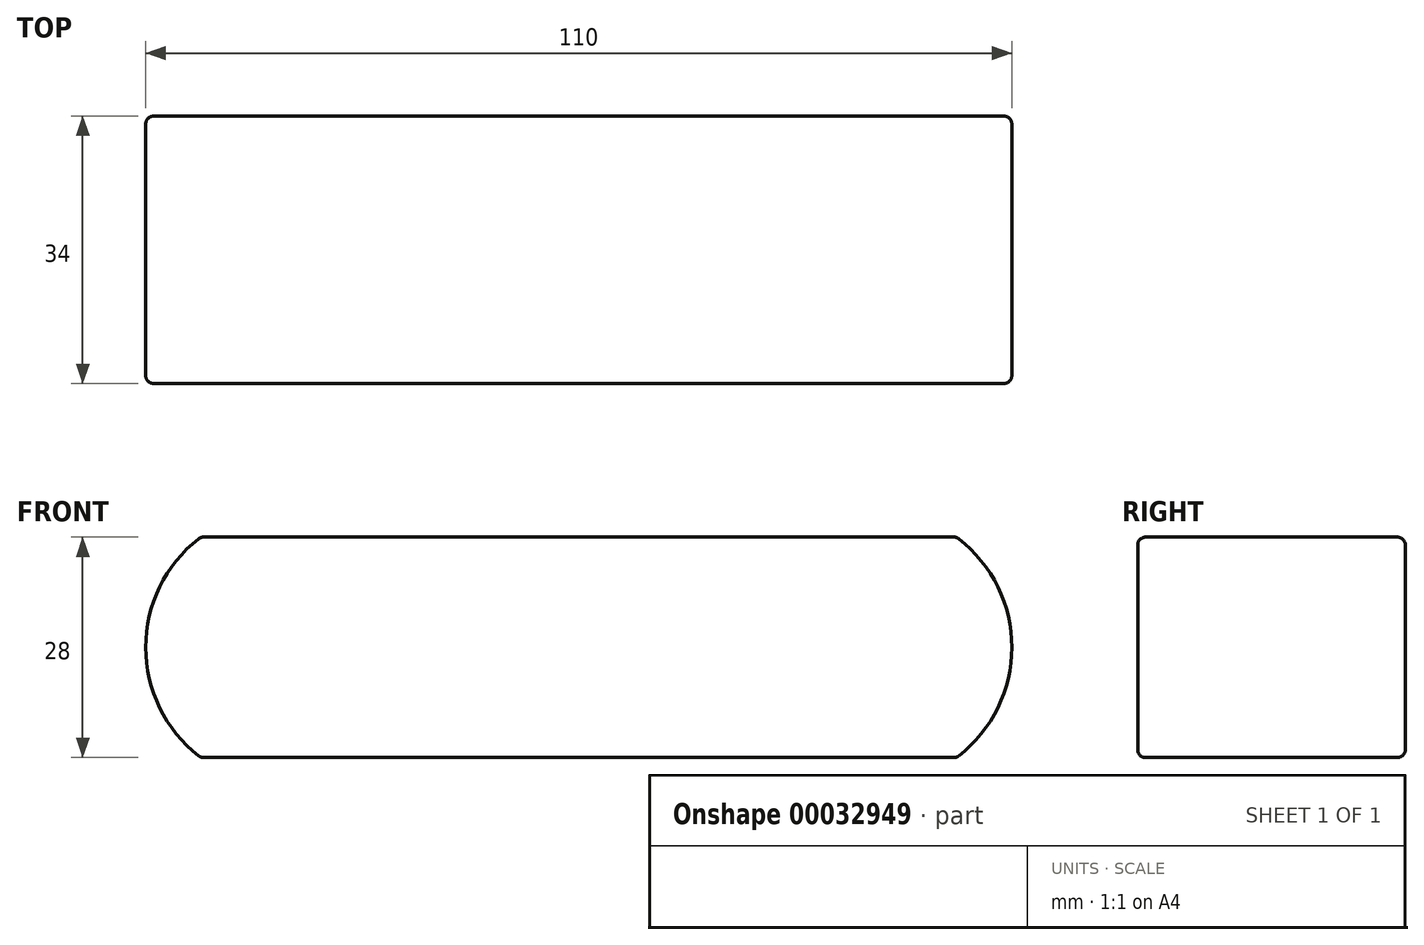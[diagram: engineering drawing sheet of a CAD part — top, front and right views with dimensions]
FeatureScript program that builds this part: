
annotation { "Feature Type Name" : "Feature", "Feature Type Description" : "" }
export const myFeature = defineFeature(function(context is Context, id is Id, definition is map)
    precondition{}
    {
        {
            var Q0;
            Q0=qCreatedBy(makeId("Front.planeOp"),FACE);
            var sketch = newSketch(context, id + "F0", { "sketchPlane" : qUnion([Q0])});
            skLineSegment(sketch, "E0.rect.bottom", {"start": v(48, -14) * mm, "end": v(-48, -14) * mm});
            skLineSegment(sketch, "E0.rect.top", {"start": v(48, 14) * mm, "end": v(-48, 14) * mm});
            skPoint(sketch, "E0.rect.middle", {"position": v(0, 0) * mm});
            skLineSegment(sketch, "E1.rect.bottom", {"start": v(55, -14) * mm, "end": v(-55, -14) * mm, "construction": true});
            skLineSegment(sketch, "E1.rect.top", {"start": v(55, 14) * mm, "end": v(-55, 14) * mm, "construction": true});
            skLineSegment(sketch, "E1.rect.left", {"start": v(55, -14) * mm, "end": v(55, 14) * mm, "construction": true});
            skLineSegment(sketch, "E1.rect.right", {"start": v(-55, -14) * mm, "end": v(-55, 14) * mm, "construction": true});
            skArc(sketch, "E2", {"start": v(48, -14) * mm, "mid": v(55, 0) * mm, "end": v(48, 14) * mm});
            skArc(sketch, "E3.MirrorCS", {"start": v(-48, -14) * mm, "mid": v(-55, 0) * mm, "end": v(-48, 14) * mm});
            skSolve(sketch);
        }
        {
            var Q0;
            Q0 = qSketchRegion(id + "F0", true);
            extrude(context, id + "F1", {"entities" : qUnion([Q0]), "depth" : 34 * mm});
        }
        {
            var Q0;
            Q0=makeQuery(id+"F1.opExtrude","CAP_FACE",FACE,{"disambiguationData":[OSD([sQuery(id+"F0.wireOp",EDGE,"E0.rect.bottom"),sQuery(id+"F0.wireOp",EDGE,"E0.rect.top"),sQuery(id+"F0.wireOp",EDGE,"E2"),sQuery(id+"F0.wireOp",EDGE,"E3.MirrorCS")])],"isStart":false});
            var Q1;
            Q1=makeQuery(id+"F1.opExtrude","CAP_FACE",FACE,{"disambiguationData":[OSD([sQuery(id+"F0.wireOp",EDGE,"E0.rect.bottom"),sQuery(id+"F0.wireOp",EDGE,"E0.rect.top"),sQuery(id+"F0.wireOp",EDGE,"E2"),sQuery(id+"F0.wireOp",EDGE,"E3.MirrorCS")])],"isStart":true});
            var Q2;
            Q2=makeQuery(id+"F1.opExtrude","SWEPT_FACE",FACE,{"disambiguationData":[OSD([sQuery(id+"F0.wireOp",EDGE,"E0.rect.top")])]});
            var Q3;
            Q3=makeQuery(id+"F1.opExtrude","SWEPT_FACE",FACE,{"disambiguationData":[OSD([sQuery(id+"F0.wireOp",EDGE,"E0.rect.bottom")])]});
            fillet(context, id + "F2", {"entities" : qUnion([Q0, Q1, Q2, Q3]), "radius" : 1 * mm, "tangentPropagation" : true, "allowEdgeOverflow" : false});
        }
    });
